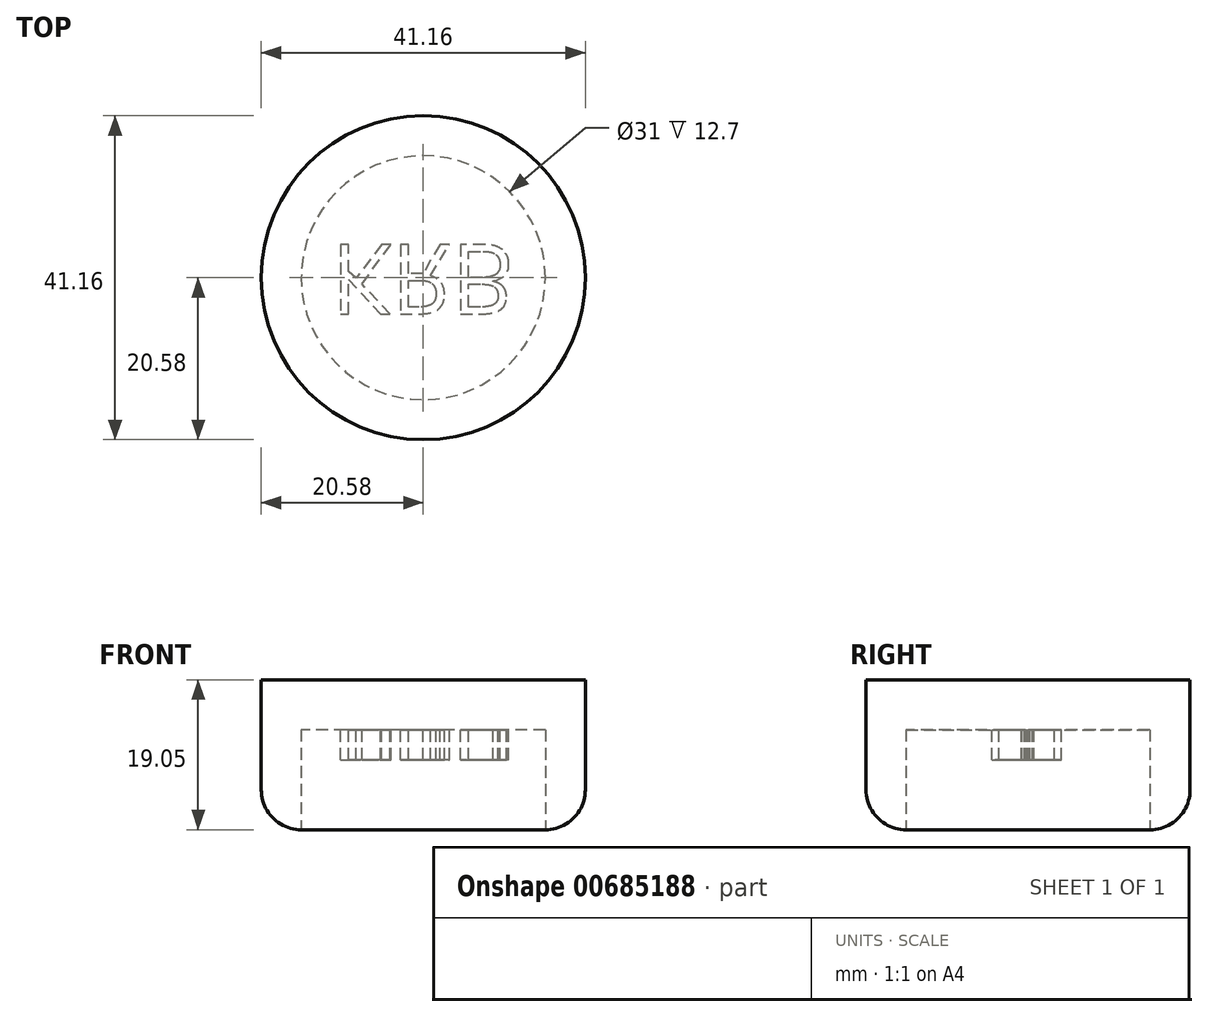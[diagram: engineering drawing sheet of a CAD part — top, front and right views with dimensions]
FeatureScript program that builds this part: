
annotation { "Feature Type Name" : "Feature", "Feature Type Description" : "" }
export const myFeature = defineFeature(function(context is Context, id is Id, definition is map)
    precondition{}
    {
        {
            var Q0;
            Q0=qCreatedBy(makeId("Top.planeOp"),FACE);
            var sketch = newSketch(context, id + "F0", { "sketchPlane" : qUnion([Q0])});
            skCircle(sketch, "E0", {"center": v(0, 0) * mm, "radius": 20.58 * mm});
            skSolve(sketch);
        }
        {
            var Q0;
            Q0=makeQuery(id+"F0.imprint","IMPRINT",FACE,{"disambiguationData":[TD([[makeQuery(id+"F0.imprint","IMPRINT",EDGE,{"derivedFrom":sQuery(id+"F0.wireOp",EDGE,"E0")}),1.0]])]});
            extrude(context, id + "F1", {"entities" : qUnion([Q0]), "oppositeDirection" : true, "depth" : 19.05 * mm, "offsetDistance" : 25.4 * mm});
        }
        {
            var Q0;
            Q0=qCreatedBy(makeId("Right.planeOp"),FACE);
            var sketch = newSketch(context, id + "F2", { "sketchPlane" : qUnion([Q0])});
            skLineSegment(sketch, "E1", {"start": v(0, 0) * mm, "end": v(0, 25.43) * mm});
            skSolve(sketch);
        }
        {
            var Q0;
            Q0=qCreatedBy(makeId("Right.planeOp"),FACE);
            var sketch = newSketch(context, id + "F3", { "sketchPlane" : qUnion([Q0])});
            skLineSegment(sketch, "E2", {"start": v(0, 25.61) * mm, "end": v(19.92, 0) * mm});
            skSolve(sketch);
        }
        {
            var Q0;
            Q0=sQuery(id+"F3.wireOp",EDGE,"E2");
            var Q1;
            Q1=sQuery(id+"F2.wireOp",EDGE,"E1");
            revolve(context, id + "F4", {"bodyType" : ToolBodyType.SURFACE, "surfaceEntities" : qUnion([Q0]), "axis" : qUnion([Q1]), "revolveType" : RevolveType.FULL});
        }
        {
            var Q0;
            Q0=makeQuery(id+"F1.opExtrude","CAP_FACE",FACE,{"disambiguationData":[OSD([sQuery(id+"F0.wireOp",EDGE,"E0")])],"isStart":false});
            fillet(context, id + "F5", {"entities" : qUnion([Q0]), "radius" : 5.08 * mm, "tangentPropagation" : true, "allowEdgeOverflow" : false});
        }
        {
            var Q0;
            Q0=makeQuery(id+"F1.opExtrude","CAP_FACE",FACE,{"disambiguationData":[OSD([sQuery(id+"F0.wireOp",EDGE,"E0")])],"isStart":false});
            extrude(context, id + "F6", {"entities" : qUnion([Q0]), "operationType" : NewBodyOperationType.REMOVE, "oppositeDirection" : true, "depth" : 12.7 * mm, "offsetDistance" : 25.4 * mm});
        }
        {
            var Q0;
            Q0=makeQuery(id+"F6.boolean.opBoolean","COPY",FACE,{"derivedFrom":makeQuery(id+"F6.opExtrude","CAP_FACE",FACE,{"disambiguationData":[OSD([sQuery(id+"F0.wireOp",EDGE,"E0")])],"isStart":false})});
            var sketch = newSketch(context, id + "F7", { "sketchPlane" : qUnion([Q0])});
            skText(sketch, "E3", { "text": "KRB", "fontName": "OpenSans-Regular.ttf"});
            const initialGuessF7  = {"E3": [-0.0117, -0.00422, 1, 0, 0.0089]};
            skSetInitialGuess(sketch, initialGuessF7);
            skSolve(sketch);
        }
        {
            var Q0;
            Q0 = qSketchRegion(id + "F7", true);
            extrude(context, id + "F8", {"entities" : qUnion([Q0]), "operationType" : NewBodyOperationType.ADD, "depth" : 3.8 * mm, "offsetDistance" : 25.4 * mm});
        }
    });
